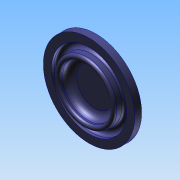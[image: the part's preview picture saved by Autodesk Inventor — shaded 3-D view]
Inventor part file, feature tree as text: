
AUTODESK INVENTOR PART (.ipt)
format: ipt  version: 2015 (Build 190159000, 159)  size: 221,696 bytes
history: native  units: mm
features: sketch x2, revolve x1
ambient origin geometry x8: Origin, YZ Plane, XZ Plane, XY Plane, X Axis, Y Axis, Z Axis, Center Point
bodies: Solid1 (feature_tree)
feature tree (3):
  sketch  "Skizze4"  dims[d2=3.45mm d3=3.5mm d4=1.6mm d5=9.0mm d6=0.45mm d7=9.0mm d8=3.5mm d9=5.75mm d10=1.25mm d11=2.2mm d12=22.5mm d13=16.75mm d14=18.5mm d22=0.45mm d25=0.45mm d26=0.45mm d28=0.7mm d29=2.45mm d30=3.0mm]
  revolve  "Revolution1"  [1 undecoded]
  sketch  "Sketch_2"  dims[d0=360.0deg d1=4.0mm]
note: 1 required parameter value undecoded (feature->parameter linkage not recoverable at this tier; creation-order binding heuristic only, values carry confidence <= 0.55)
